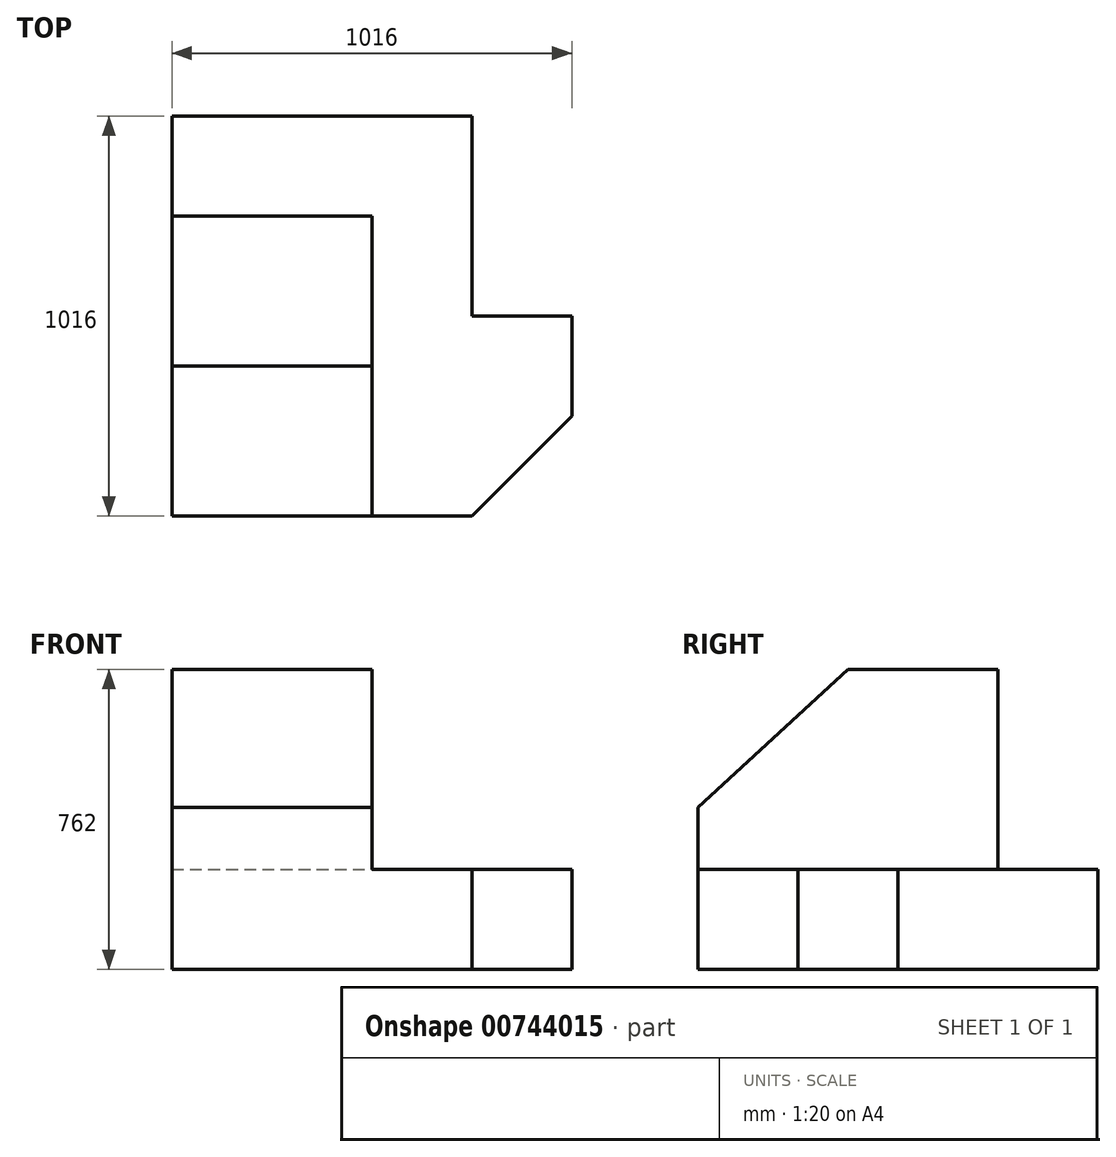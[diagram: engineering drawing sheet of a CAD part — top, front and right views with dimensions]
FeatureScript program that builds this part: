
annotation { "Feature Type Name" : "Feature", "Feature Type Description" : "" }
export const myFeature = defineFeature(function(context is Context, id is Id, definition is map)
    precondition{}
    {
        {
            var Q0;
            Q0=qCreatedBy(makeId("Front.planeOp"),FACE);
            var sketch = newSketch(context, id + "F0", { "sketchPlane" : qUnion([Q0])});
            skLineSegment(sketch, "E0.bottom", {"start": v(-507.56, 247.18) * mm, "end": v(508.44, 247.18) * mm});
            skLineSegment(sketch, "E0.top", {"start": v(-507.56, -514.82) * mm, "end": v(508.44, -514.82) * mm});
            skLineSegment(sketch, "E0.left", {"start": v(-507.56, 247.18) * mm, "end": v(-507.56, -514.82) * mm});
            skLineSegment(sketch, "E0.right", {"start": v(508.44, 247.18) * mm, "end": v(508.44, -514.82) * mm});
            skSolve(sketch);
        }
        {
            var Q0;
            Q0 = qSketchRegion(id + "F0", true);
            extrude(context, id + "F1", {"entities" : qUnion([Q0]), "depth" : 1016 * mm, "offsetDistance" : 25 * mm});
        }
        {
            var Q0;
            Q0=makeQuery(id+"F1.opExtrude","SWEPT_FACE",FACE,{"disambiguationData":[OSD([sQuery(id+"F0.wireOp",EDGE,"E0.bottom")])]});
            var sketch = newSketch(context, id + "F2", { "sketchPlane" : qUnion([Q0])});
            skLineSegment(sketch, "E1.bottom", {"start": v(508.44, 0) * mm, "end": v(254.44, 0) * mm});
            skLineSegment(sketch, "E1.top", {"start": v(508.44, -508) * mm, "end": v(254.44, -508) * mm});
            skLineSegment(sketch, "E1.left", {"start": v(508.44, 0) * mm, "end": v(508.44, -508) * mm});
            skLineSegment(sketch, "E1.right", {"start": v(254.44, 0) * mm, "end": v(254.44, -508) * mm});
            skSolve(sketch);
        }
        {
            var Q0;
            Q0 = qSketchRegion(id + "F2", true);
            extrude(context, id + "F3", {"entities" : qUnion([Q0]), "operationType" : NewBodyOperationType.REMOVE, "oppositeDirection" : true, "depth" : 1016 * mm, "offsetDistance" : 25 * mm});
        }
        {
            var Q0;
            Q0=makeQuery(id+"F1.opExtrude","SWEPT_FACE",FACE,{"disambiguationData":[OSD([sQuery(id+"F0.wireOp",EDGE,"E0.bottom")])]});
            var sketch = newSketch(context, id + "F4", { "sketchPlane" : qUnion([Q0])});
            skLineSegment(sketch, "E2.bottom", {"start": v(-507.56, -1016) * mm, "end": v(0.44, -1016) * mm});
            skLineSegment(sketch, "E2.top", {"start": v(-507.56, -254) * mm, "end": v(0.44, -254) * mm});
            skLineSegment(sketch, "E2.left", {"start": v(-507.56, -1016) * mm, "end": v(-507.56, -254) * mm});
            skLineSegment(sketch, "E2.right", {"start": v(0.44, -1016) * mm, "end": v(0.44, -254) * mm});
            skSolve(sketch);
        }
        {
            var Q0;
            {var subQ6=sQuery(id+"F4.wireOp",EDGE,"E2.top");Q0=makeQuery(id+"F4.imprint","IMPRINT",FACE,{"disambiguationData":[TD([[makeQuery(id+"F4.imprint","IMPRINT",EDGE,{"derivedFrom":subQ6}),1.0]])]});}
            var sketch = newSketch(context, id + "F5", { "sketchPlane" : qUnion([Q0])});
            skLineSegment(sketch, "E3", {"start": v(-506.66, 0) * mm, "end": v(-506.66, -254.1) * mm});
            skLineSegment(sketch, "E4", {"start": v(-506.66, -254.1) * mm, "end": v(0, -254.1) * mm});
            skLineSegment(sketch, "E5", {"start": v(0, -1022.82) * mm, "end": v(509.7, -1022.82) * mm});
            skLineSegment(sketch, "E6", {"start": v(509.7, -1022.82) * mm, "end": v(509.7, -506.03) * mm});
            skLineSegment(sketch, "E7", {"start": v(509.7, -506.03) * mm, "end": v(268.53, -506.03) * mm});
            skLineSegment(sketch, "E8", {"start": v(268.53, -506.03) * mm, "end": v(268.53, 0) * mm});
            skLineSegment(sketch, "E9", {"start": v(268.53, 0) * mm, "end": v(-506.66, 0) * mm});
            skSolve(sketch);
        }
        {
            var Q0;
            {var subQ6=sQuery(id+"F4.wireOp",EDGE,"E2.top");Q0=makeQuery(id+"F4.imprint","IMPRINT",FACE,{"disambiguationData":[TD([[makeQuery(id+"F4.imprint","IMPRINT",EDGE,{"derivedFrom":subQ6}),1.0]])]});}
            extrude(context, id + "F6", {"entities" : qUnion([Q0]), "operationType" : NewBodyOperationType.REMOVE, "oppositeDirection" : true, "depth" : 508 * mm, "offsetDistance" : 25 * mm});
        }
        {
            var Q0;
            {var subQ3=sQuery(id+"F4.wireOp",EDGE,"E2.right");var subQ4=makeQuery(id+"F4.imprint","IMPRINT",EDGE,{"derivedFrom":subQ3});Q0=makeQuery(id+"F5.imprint","IMPRINT",FACE,{"disambiguationData":[TD([[makeQuery(id+"F5.imprint","IMPRINT",EDGE,{"derivedFrom":subQ4}),-1.0]])]});}
            extrude(context, id + "F7", {"entities" : qUnion([Q0]), "depth" : 25 * mm, "offsetDistance" : 25 * mm});
        }
        {
            var Q0;
            Q0=makeQuery(id+"F7.opExtrude","CAP_FACE",FACE,{"disambiguationData":[OSD([sQuery(id+"F0.wireOp",EDGE,"E0.bottom"),sQuery(id+"F0.wireOp",EDGE,"E0.right"),sQuery(id+"F2.wireOp",EDGE,"E1.top"),sQuery(id+"F2.wireOp",EDGE,"E1.right"),sQuery(id+"F4.wireOp",EDGE,"E2.top"),sQuery(id+"F4.wireOp",EDGE,"E2.right"),sQuery(id+"F5.wireOp",EDGE,"E3"),sQuery(id+"F5.wireOp",EDGE,"E9")])],"isStart":false});
            var sketch = newSketch(context, id + "F8", { "sketchPlane" : qUnion([Q0])});
            skSolve(sketch);
        }
        {
            var Q0;
            Q0 = qSketchRegion(id + "F8", true);
            var Q1;
            Q1=makeQuery(id+"F8.imprint","IMPRINT",FACE,{"disambiguationData":[TD([[makeQuery(id+"F8.imprint","IMPRINT",EDGE,{"derivedFrom":makeQuery(id+"F7.opExtrude","CAP_EDGE",EDGE,{"disambiguationData":[OSD([sQuery(id+"F5.wireOp",EDGE,"E3")])],"isStart":false})}),1.0]])]});
            extrude(context, id + "F9", {"entities" : qUnion([Q0, Q1]), "operationType" : NewBodyOperationType.REMOVE, "oppositeDirection" : true, "depth" : 254 * mm, "offsetDistance" : 25 * mm});
        }
        {
            var Q0;
            Q0=makeQuery(id+"F1.opExtrude","SWEPT_FACE",FACE,{"disambiguationData":[OSD([sQuery(id+"F0.wireOp",EDGE,"E0.left")])]});
            var sketch = newSketch(context, id + "F10", { "sketchPlane" : qUnion([Q0])});
            skLineSegment(sketch, "E10", {"start": v(1016, 247.18) * mm, "end": v(1016, -102.99) * mm});
            skLineSegment(sketch, "E11", {"start": v(1016, -102.99) * mm, "end": v(635, 247.18) * mm});
            skLineSegment(sketch, "E12", {"start": v(635, 247.18) * mm, "end": v(1016, 247.18) * mm});
            skSolve(sketch);
        }
        {
            var Q0;
            Q0 = qSketchRegion(id + "F10", true);
            extrude(context, id + "F11", {"entities" : qUnion([Q0]), "operationType" : NewBodyOperationType.REMOVE, "oppositeDirection" : true, "depth" : 762 * mm, "offsetDistance" : 25 * mm});
        }
        {
            var Q0;
            Q0=makeQuery(id+"F1.opExtrude","CAP_EDGE",EDGE,{"disambiguationData":[OSD([sQuery(id+"F0.wireOp",EDGE,"E0.right")])],"isStart":false});
            chamfer(context, id + "F12", {"entities" : qUnion([Q0]), "width" : 254 * mm, "tangentPropagation" : true});
        }
    });
